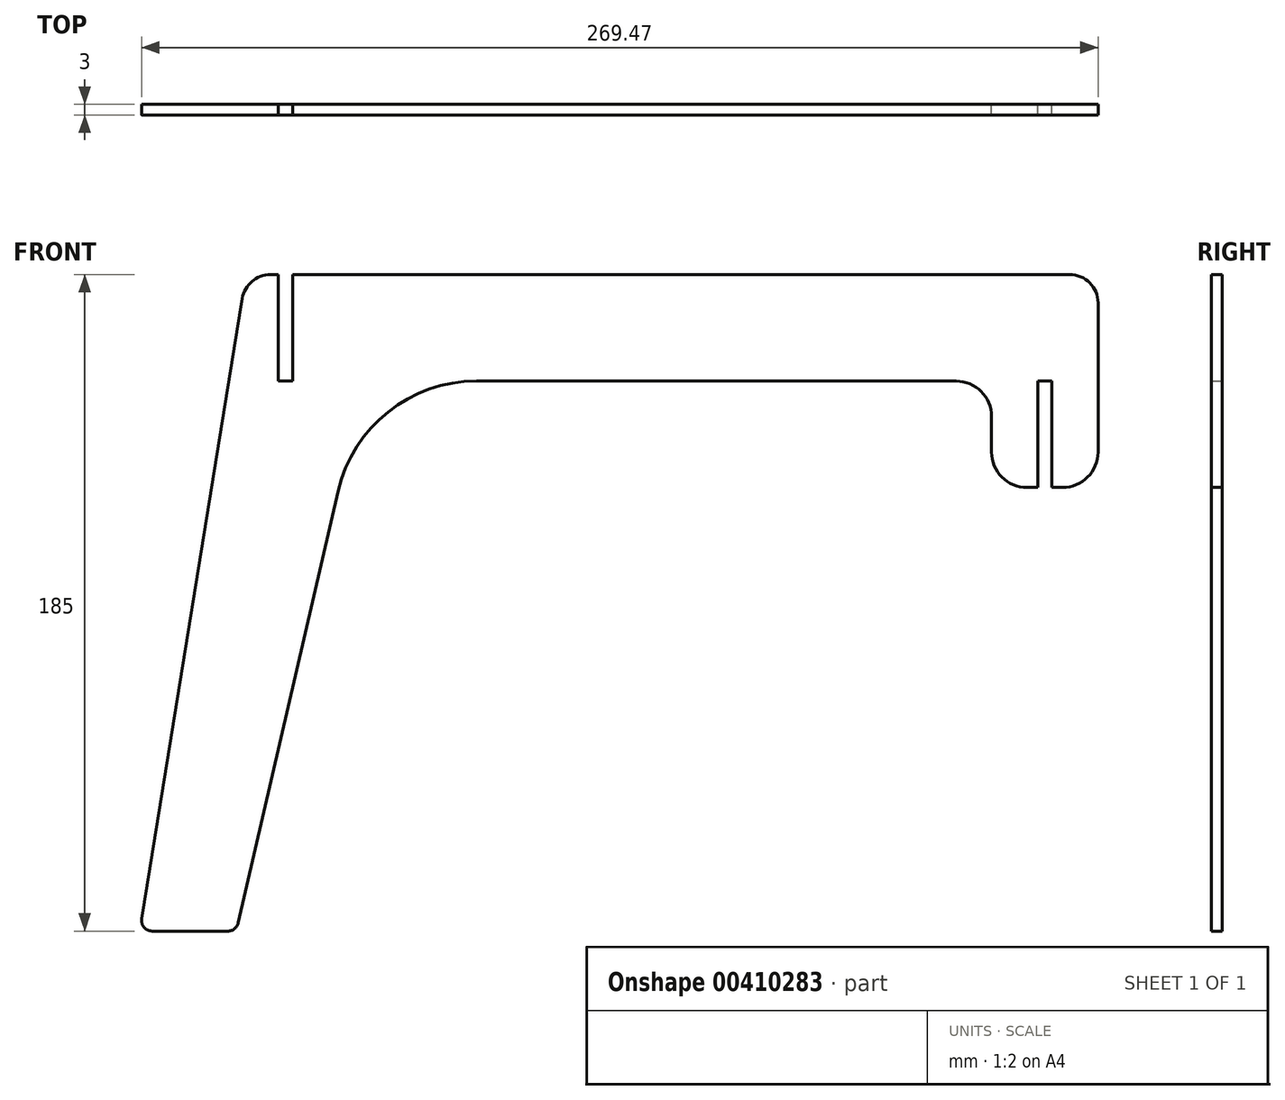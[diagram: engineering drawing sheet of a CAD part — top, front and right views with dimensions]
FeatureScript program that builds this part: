
annotation { "Feature Type Name" : "Feature", "Feature Type Description" : "" }
export const myFeature = defineFeature(function(context is Context, id is Id, definition is map)
    precondition{}
    {
        {
            var Q0;
            Q0=qCreatedBy(makeId("Front.planeOp"),FACE);
            var sketch = newSketch(context, id + "F0", { "sketchPlane" : qUnion([Q0])});
            skLineSegment(sketch, "E0.bottom", {"start": v(-98.2, 92.5) * mm, "end": v(-95.9, 92.5) * mm});
            skLineSegment(sketch, "E0.top", {"start": v(-131.47, -92.5) * mm, "end": v(-110.14, -92.5) * mm});
            skLineSegment(sketch, "E0.right", {"start": v(135, 84.5) * mm, "end": v(135, 32.5) * mm});
            skPoint(sketch, "E0.middle", {"position": v(0, 0) * mm});
            skLineSegment(sketch, "E1", {"start": v(-107.22, -90.18) * mm, "end": v(-79.1, 31.5) * mm});
            skLineSegment(sketch, "E2", {"start": v(-134.44, -89.02) * mm, "end": v(-106.09, 85.78) * mm});
            skLineSegment(sketch, "E3", {"start": v(-40.12, 62.5) * mm, "end": v(95, 62.5) * mm});
            skLineSegment(sketch, "E4", {"start": v(135, 62.5) * mm, "end": v(135, 42.5) * mm});
            skLineSegment(sketch, "E5", {"start": v(125, 32.5) * mm, "end": v(122, 32.5) * mm});
            skLineSegment(sketch, "E6", {"start": v(105, 42.5) * mm, "end": v(105, 52.5) * mm});
            skPoint(sketch, "E7.orphan", {"position": v(135, -92.5) * mm});
            skPoint(sketch, "E8.orphan", {"position": v(-135, 92.5) * mm});
            skPoint(sketch, "E9.orphan", {"position": v(-65, 92.5) * mm});
            skLineSegment(sketch, "E10", {"start": v(-95.9, 92.5) * mm, "end": v(-95.9, 62.5) * mm});
            skLineSegment(sketch, "E11", {"start": v(-95.9, 62.5) * mm, "end": v(-91.9, 62.5) * mm});
            skLineSegment(sketch, "E12", {"start": v(-91.9, 62.5) * mm, "end": v(-91.9, 92.5) * mm});
            skLineSegment(sketch, "E13", {"start": v(118, 32.5) * mm, "end": v(118, 62.5) * mm});
            skLineSegment(sketch, "E14", {"start": v(118, 62.5) * mm, "end": v(122, 62.5) * mm});
            skLineSegment(sketch, "E15", {"start": v(122, 62.5) * mm, "end": v(122, 32.5) * mm});
            skLineSegment(sketch, "E16.trimOffspring", {"start": v(-91.9, 92.5) * mm, "end": v(127, 92.5) * mm});
            skLineSegment(sketch, "E17.trimOffspring", {"start": v(118, 32.5) * mm, "end": v(115, 32.5) * mm});
            skPoint(sketch, "E18.visualSharp", {"position": v(-71.93, 62.5) * mm});
            skArc(sketch, "E18.filletArc", {"start": v(-40.12, 62.5) * mm, "mid": v(-65.02, 53.8) * mm, "end": v(-79.1, 31.5) * mm});
            skPoint(sketch, "E19.visualSharp", {"position": v(105, 62.5) * mm});
            skArc(sketch, "E19.filletArc", {"start": v(105, 52.5) * mm, "mid": v(102.07, 59.57) * mm, "end": v(95, 62.5) * mm});
            skPoint(sketch, "E20.visualSharp", {"position": v(105, 32.5) * mm});
            skArc(sketch, "E20.filletArc", {"start": v(105, 42.5) * mm, "mid": v(107.93, 35.43) * mm, "end": v(115, 32.5) * mm});
            skPoint(sketch, "E21.visualSharp", {"position": v(135, 32.5) * mm});
            skArc(sketch, "E21.filletArc", {"start": v(125, 32.5) * mm, "mid": v(132.07, 35.43) * mm, "end": v(135, 42.5) * mm});
            skPoint(sketch, "E22.visualSharp", {"position": v(135, 92.5) * mm});
            skArc(sketch, "E22.filletArc", {"start": v(135, 84.5) * mm, "mid": v(132.66, 90.16) * mm, "end": v(127, 92.5) * mm});
            skPoint(sketch, "E23.visualSharp", {"position": v(-107.76, -92.5) * mm});
            skArc(sketch, "E23.filletArc", {"start": v(-110.14, -92.5) * mm, "mid": v(-108.27, -91.85) * mm, "end": v(-107.22, -90.18) * mm});
            skPoint(sketch, "E24.visualSharp", {"position": v(-135, -92.5) * mm});
            skArc(sketch, "E24.filletArc", {"start": v(-134.44, -89.02) * mm, "mid": v(-133.76, -91.44) * mm, "end": v(-131.47, -92.5) * mm});
            skPoint(sketch, "E25.visualSharp", {"position": v(-105, 92.5) * mm});
            skArc(sketch, "E25.filletArc", {"start": v(-98.2, 92.5) * mm, "mid": v(-103.38, 90.6) * mm, "end": v(-106.09, 85.78) * mm});
            skSolve(sketch);
        }
        {
            var Q0;
            Q0=makeQuery(id+"F0.imprint","IMPRINT",FACE,{"disambiguationData":[TD([[makeQuery(id+"F0.imprint","IMPRINT",EDGE,{"derivedFrom":sQuery(id+"F0.wireOp",EDGE,"E0.bottom")}),-1.0]])]});
            extrude(context, id + "F1", {"entities" : qUnion([Q0]), "depth" : 3 * mm});
        }
    });
